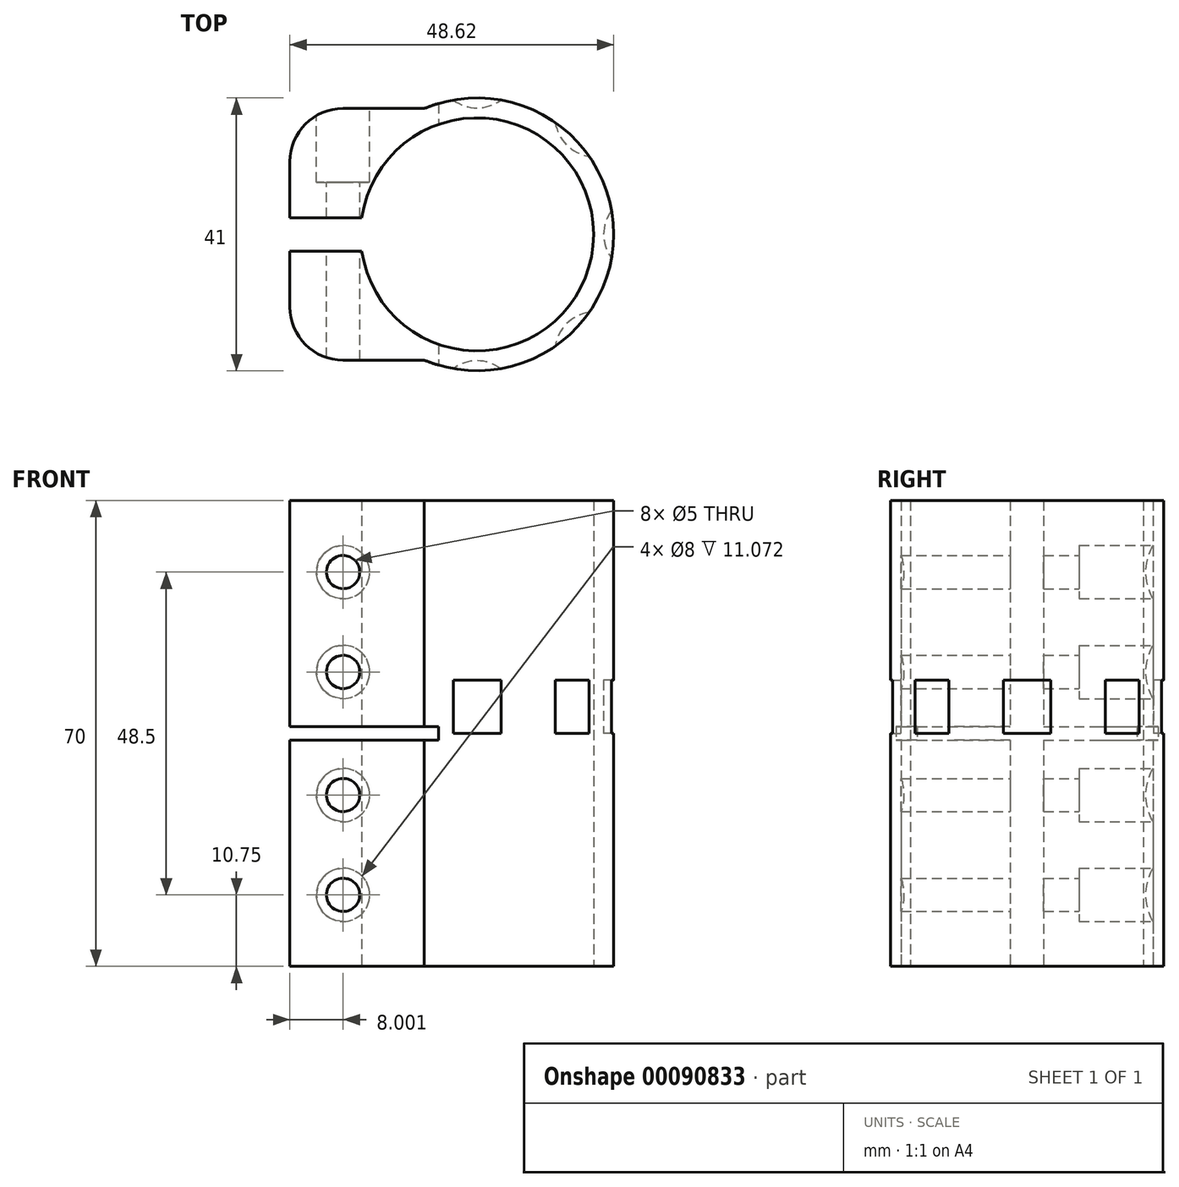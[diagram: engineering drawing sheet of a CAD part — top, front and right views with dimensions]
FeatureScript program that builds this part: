
annotation { "Feature Type Name" : "Feature", "Feature Type Description" : "" }
export const myFeature = defineFeature(function(context is Context, id is Id, definition is map)
    precondition{}
    {
        {
            var Q0;
            Q0=qCreatedBy(makeId("Top.planeOp"),FACE);
            var sketch = newSketch(context, id + "F0", { "sketchPlane" : qUnion([Q0])});
            skArc(sketch, "E0", {"start": v(-17.32, -2.5) * mm, "mid": v(17.5, 0) * mm, "end": v(-17.32, 2.5) * mm});
            skArc(sketch, "E1", {"start": v(-7.92, -18.9) * mm, "mid": v(20.5, 0) * mm, "end": v(-7.92, 18.9) * mm});
            skLineSegment(sketch, "E2", {"start": v(-7.92, 18.9) * mm, "end": v(-20.12, 18.9) * mm});
            skLineSegment(sketch, "E3", {"start": v(-28.12, 10.9) * mm, "end": v(-28.12, 2.5) * mm});
            skLineSegment(sketch, "E4", {"start": v(-28.12, 2.5) * mm, "end": v(-20.35, 2.5) * mm});
            skPoint(sketch, "E5.visualSharp", {"position": v(-28.12, 18.9) * mm});
            skArc(sketch, "E5.filletArc", {"start": v(-20.12, 18.9) * mm, "mid": v(-25.78, 16.57) * mm, "end": v(-28.12, 10.9) * mm});
            skLineSegment(sketch, "E6", {"start": v(-20.35, 2.5) * mm, "end": v(-17.32, 2.5) * mm});
            skLineSegment(sketch, "E7", {"start": v(0, 0) * mm, "end": v(55.56, 0) * mm, "construction": true});
            skLineSegment(sketch, "E8.MirrorCS", {"start": v(-20.35, -2.5) * mm, "end": v(-17.32, -2.5) * mm});
            skPoint(sketch, "E9.MirrorP", {"position": v(-28.12, -18.9) * mm});
            skLineSegment(sketch, "E10.MirrorCS", {"start": v(-28.12, -10.9) * mm, "end": v(-28.12, -2.5) * mm});
            skLineSegment(sketch, "E11.MirrorCS", {"start": v(-28.12, -2.5) * mm, "end": v(-20.35, -2.5) * mm});
            skArc(sketch, "E12.MirrorCS", {"start": v(-20.12, -18.9) * mm, "mid": v(-25.78, -16.57) * mm, "end": v(-28.12, -10.9) * mm});
            skLineSegment(sketch, "E13.MirrorCS", {"start": v(-7.92, -18.9) * mm, "end": v(-20.12, -18.9) * mm});
            skSolve(sketch);
        }
        {
            var Q0;
            Q0 = qSketchRegion(id + "F0", true);
            extrude(context, id + "F1", {"entities" : qUnion([Q0]), "endBound" : BoundingType.SYMMETRIC, "depth" : 70 * mm});
        }
        {
            var Q0;
            Q0=makeQuery(id+"F1.opExtrude","SWEPT_FACE",FACE,{"disambiguationData":[OSD([sQuery(id+"F0.wireOp",EDGE,"E2")])]});
            var sketch = newSketch(context, id + "F2", { "sketchPlane" : qUnion([Q0])});
            skPoint(sketch, "E14", {"position": v(20.12, -24.25) * mm});
            skPoint(sketch, "E15", {"position": v(20.12, -9.25) * mm});
            skPoint(sketch, "E16", {"position": v(20.12, 9.25) * mm});
            skPoint(sketch, "E17", {"position": v(20.12, 24.25) * mm});
            skSolve(sketch);
        }
        {
            var Q0;
            Q0=sQuery(id+"F2.wireOp",VERTEX,"E17");
            var Q1;
            Q1=sQuery(id+"F2.wireOp",VERTEX,"E16");
            var Q2;
            Q2=sQuery(id+"F2.wireOp",VERTEX,"E15");
            var Q3;
            Q3=sQuery(id+"F2.wireOp",VERTEX,"E14");
            var Q4;
            Q4=makeQuery(id+"F1.opExtrude","SWEPT_BODY",BODY,{"disambiguationData":[OSD([sQuery(id+"F0.wireOp",EDGE,"E0"),sQuery(id+"F0.wireOp",EDGE,"E1"),sQuery(id+"F0.wireOp",EDGE,"E2"),sQuery(id+"F0.wireOp",EDGE,"E3"),sQuery(id+"F0.wireOp",EDGE,"E4"),sQuery(id+"F0.wireOp",EDGE,"E5.filletArc"),sQuery(id+"F0.wireOp",EDGE,"E6"),sQuery(id+"F0.wireOp",EDGE,"E8.MirrorCS"),sQuery(id+"F0.wireOp",EDGE,"E10.MirrorCS"),sQuery(id+"F0.wireOp",EDGE,"E11.MirrorCS"),sQuery(id+"F0.wireOp",EDGE,"E12.MirrorCS"),sQuery(id+"F0.wireOp",EDGE,"E13.MirrorCS")])]});
            hole(context, id + "F3", {"style" : HoleStyle.C_BORE, "endStyle" : HoleEndStyle.THROUGH, "holeDiameter" : 5 * mm, "cBoreDiameter" : 8 * mm, "cBoreDepth" : 10 * mm, "locations" : qUnion([Q0, Q1, Q2, Q3]), "scope" : qUnion([Q4]), "isTappedThrough" : true});
        }
        {
            var Q0;
            Q0=qCreatedBy(makeId("Front.planeOp"),FACE);
            var sketch = newSketch(context, id + "F4", { "sketchPlane" : qUnion([Q0])});
            skLineSegment(sketch, "E18.bottom", {"start": v(-28.2, 1) * mm, "end": v(-5.8, 1) * mm});
            skLineSegment(sketch, "E18.top", {"start": v(-28.2, -1) * mm, "end": v(-5.8, -1) * mm});
            skLineSegment(sketch, "E18.left", {"start": v(-28.2, 1) * mm, "end": v(-28.2, -1) * mm});
            skLineSegment(sketch, "E18.right", {"start": v(-5.8, 1) * mm, "end": v(-5.8, -1) * mm});
            skSolve(sketch);
        }
        {
            var Q0;
            Q0 = qSketchRegion(id + "F4", true);
            extrude(context, id + "F5", {"entities" : qUnion([Q0]), "operationType" : NewBodyOperationType.REMOVE, "endBound" : BoundingType.SYMMETRIC, "oppositeDirection" : true, "depth" : 50 * mm});
        }
        {
            var Q0;
            Q0=qCreatedBy(makeId("Top.planeOp"),FACE);
            var sketch = newSketch(context, id + "F6", { "sketchPlane" : qUnion([Q0])});
            skCircle(sketch, "E19", {"center": v(0, -25) * mm, "radius": 6 * mm});
            skCircle(sketch, "E20.1.0", {"center": v(17.68, -17.68) * mm, "radius": 6 * mm});
            skCircle(sketch, "E20.2.0", {"center": v(25, 0) * mm, "radius": 6 * mm});
            skCircle(sketch, "E20.3.0", {"center": v(17.68, 17.68) * mm, "radius": 6 * mm});
            skCircle(sketch, "E20.4.0", {"center": v(0, 25) * mm, "radius": 6 * mm});
            skPoint(sketch, "E20.center", {"position": v(0, 0) * mm});
            skLineSegment(sketch, "E20.anchor1", {"start": v(0, 0) * mm, "end": v(0, -25) * mm, "construction": true});
            skLineSegment(sketch, "E20.anchor2", {"start": v(0, 0) * mm, "end": v(0, 25) * mm, "construction": true});
            skSolve(sketch);
        }
        {
            var Q0;
            Q0=makeQuery(id+"F6.imprint","IMPRINT",FACE,{"disambiguationData":[TD([[makeQuery(id+"F6.imprint","IMPRINT",EDGE,{"derivedFrom":sQuery(id+"F6.wireOp",EDGE,"E20.3.0")}),1.0]])]});
            var Q1;
            Q1=makeQuery(id+"F6.imprint","IMPRINT",FACE,{"disambiguationData":[TD([[makeQuery(id+"F6.imprint","IMPRINT",EDGE,{"derivedFrom":sQuery(id+"F6.wireOp",EDGE,"E20.4.0")}),1.0]])]});
            var Q2;
            Q2=makeQuery(id+"F6.imprint","IMPRINT",FACE,{"disambiguationData":[TD([[makeQuery(id+"F6.imprint","IMPRINT",EDGE,{"derivedFrom":sQuery(id+"F6.wireOp",EDGE,"E20.2.0")}),1.0]])]});
            var Q3;
            Q3=makeQuery(id+"F6.imprint","IMPRINT",FACE,{"disambiguationData":[TD([[makeQuery(id+"F6.imprint","IMPRINT",EDGE,{"derivedFrom":sQuery(id+"F6.wireOp",EDGE,"E20.1.0")}),1.0]])]});
            var Q4;
            Q4=makeQuery(id+"F6.imprint","IMPRINT",FACE,{"disambiguationData":[TD([[makeQuery(id+"F6.imprint","IMPRINT",EDGE,{"derivedFrom":sQuery(id+"F6.wireOp",EDGE,"E19")}),1.0]])]});
            extrude(context, id + "F7", {"entities" : qUnion([Q0, Q1, Q2, Q3, Q4]), "operationType" : NewBodyOperationType.REMOVE, "depth" : 8 * mm});
        }
    });
